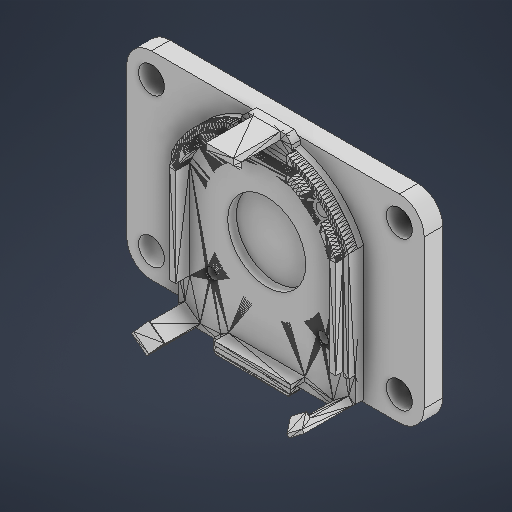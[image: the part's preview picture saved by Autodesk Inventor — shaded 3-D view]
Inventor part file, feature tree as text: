
AUTODESK INVENTOR PART (.ipt)
format: ipt  version: 2025 (Build 290162000, 162)  size: 1,869,312 bytes
history: native  units: in
note: dims shown in document units (in); Inventor stores cm internally (conversion verified against a paired STEP export)
features: extrude x7, sketch x5, plane x1, fillet x1, other x1
ambient origin geometry x8: Origin, YZ Plane, XZ Plane, XY Plane, X Axis, Y Axis, Z Axis, Center Point
bodies: Solid1 (feature_tree)
feature tree (15):
  plane  "Work Plane1"
  extrude  "Extrusion1"  Depth=0.1575in
  extrude  "Extrusion2"  Depth=0.4961in
  sketch  "Sketch3"  dims[d5=0.3937in d6=0.0in d7=0.0787in]
  extrude  "Extrusion3"  Depth=0.3937in
  extrude  "Extrusion4"  TaperAngle=0.0deg  [1 undecoded]
  sketch  "Sketch4"  dims[d8=0.1181in d9=0.0in d10=0.0in]
  extrude  "Extrusion5"  Depth=0.1575in
  extrude  "Extrusion6"  Depth=0.1575in
  extrude  "Extrusion7"  Depth=0.1575in
  fillet  "Fillet1"  Radius=0.0591in
  sketch  "Sketch1"  dims[d0=0.4803in d1=0.1575in]
  sketch  "Sketch2"  dims[d2=0.0in d3=0.0in d4=0.4961in]
  sketch  "Sketch5"  dims[d11=0.3937in d12=0.0in d13=0.0787in d14=0.0787in d15=0.0787in d16=0.0591in d17=0.0591in d18=0.0591in d19=0.0079in d20=0.0079in d21=0.0079in d22=0.0394in d23=0.0in d24=0.0394in d25=0.0in d26=1.2598in d27=1.8898in d28=1.2598in d29=0.1654in d30=0.7874in d31=0.4724in d32=0.1181in d33=0.0in d34=0.1575in]
  other  "MeshFeature1"
note: 1 required parameter value undecoded (feature->parameter linkage not recoverable at this tier; creation-order binding heuristic only, values carry confidence <= 0.55)
